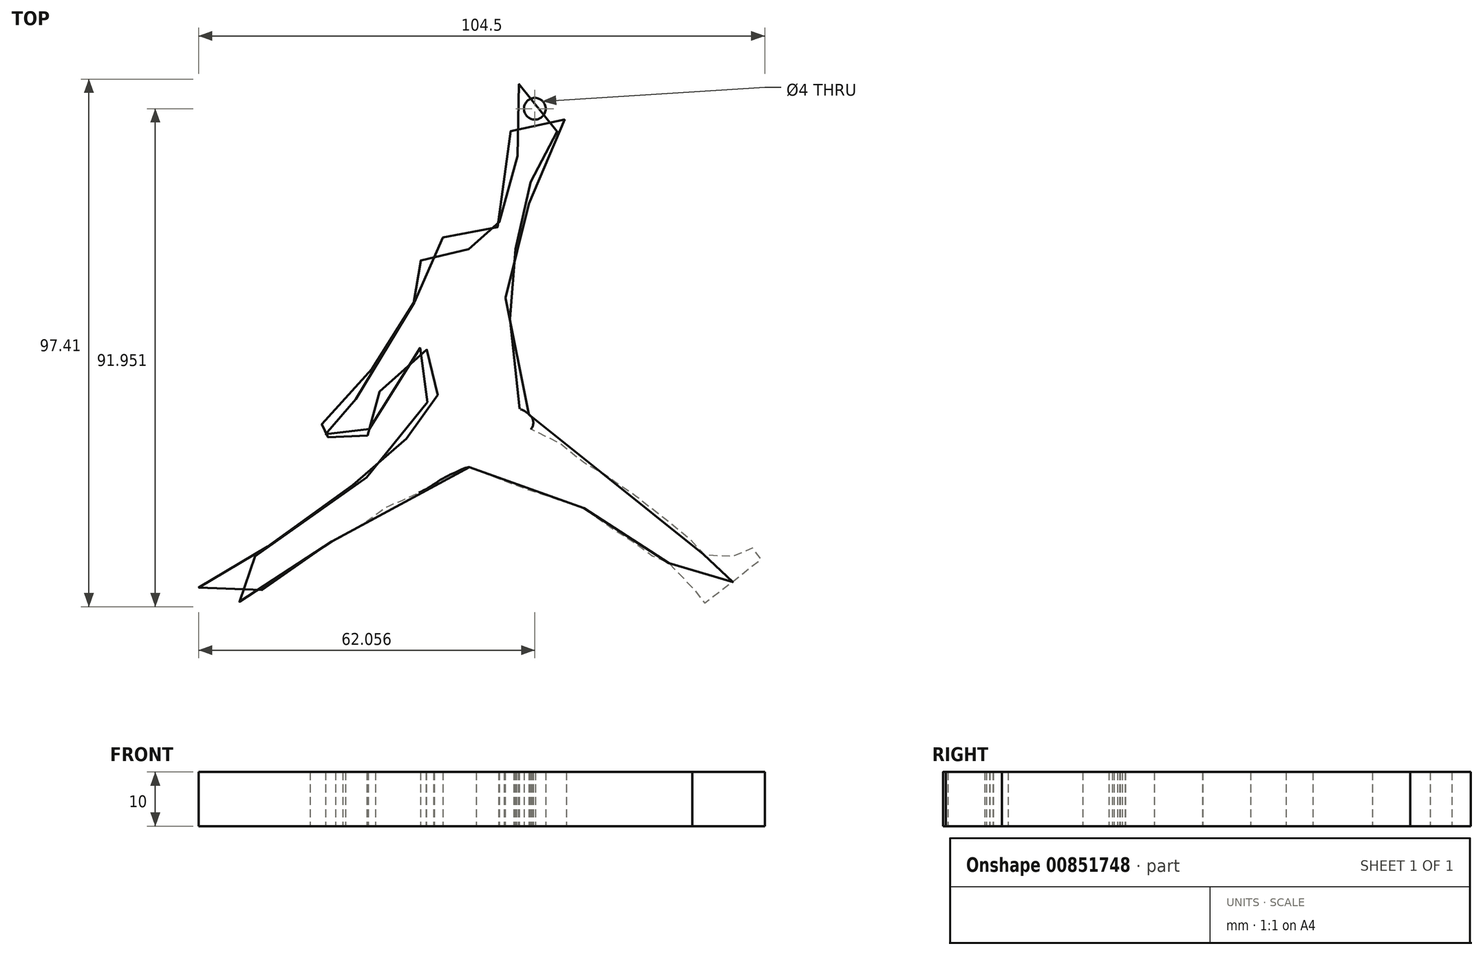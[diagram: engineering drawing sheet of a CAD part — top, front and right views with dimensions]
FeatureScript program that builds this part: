
annotation { "Feature Type Name" : "Feature", "Feature Type Description" : "" }
export const myFeature = defineFeature(function(context is Context, id is Id, definition is map)
    precondition{}
    {
        {
            var Q0;
            Q0=qCreatedBy(makeId("Top.planeOp"),FACE);
            var sketch = newSketch(context, id + "F0", { "sketchPlane" : qUnion([Q0])});
            skFitSpline(sketch, "E0", {"points": [v(0, -19.8) * mm, v(0.2, -19.83) * mm, v(0.48, -19.99) * mm, v(1.1, -20.32) * mm, v(2.32, -20.88) * mm, v(3.56, -21.27) * mm, v(5.27, -21.74) * mm, v(7.68, -22.78) * mm, v(9.68, -23.51) * mm, v(11.32, -24.32) * mm, v(13.95, -25.3) * mm, v(15.3, -25.56) * mm, v(18.19, -26.14) * mm, v(19.48, -26.44) * mm, v(19.57, -26.65) * mm, v(20.06, -26.91) * mm, v(21.05, -27.34) * mm, v(22.12, -27.94) * mm, v(23.74, -29.2) * mm, v(25.71, -30.67) * mm, v(27.3, -31.83) * mm, v(28.82, -33.03) * mm, v(29.33, -33.3) * mm, v(29.66, -33.44) * mm, v(30.19, -33.56) * mm, v(30.42, -33.56) * mm, v(31.1, -34.2) * mm, v(32.19, -34.96) * mm, v(33.13, -35.66) * mm, v(34.06, -36.37) * mm, v(34.75, -36.83) * mm, v(35.13, -36.98) * mm, v(35.58, -36.98) * mm, v(35.91, -36.98) * mm, v(36.16, -36.98) * mm, v(36.7, -37.44) * mm, v(37.25, -37.84) * mm, v(37.4, -38.04) * mm, v(37.53, -38.3) * mm, v(37.79, -38.55) * mm, v(38.11, -38.88) * mm, v(38.42, -39.16) * mm, v(38.8, -39.59) * mm, v(39.15, -39.72) * mm, v(39.3, -40) * mm, v(39.44, -40.32) * mm, v(40.42, -41.42) * mm, v(40.69, -41.76) * mm, v(41.12, -42) * mm, v(41.13, -42.31) * mm, v(41.37, -42.96) * mm, v(41.75, -43.62) * mm, v(42.58, -45) * mm, v(43.18, -45) * mm, v(44.19, -44.26) * mm, v(45.57, -43.07) * mm, v(47.18, -41.78) * mm, v(49.3, -40.67) * mm, v(51.32, -39.06) * mm, v(52.93, -37.54) * mm, v(54.5, -35.98) * mm, v(54.31, -35.5) * mm, v(53.92, -35.14) * mm, v(53.48, -34.9) * mm, v(52.87, -34.71) * mm, v(52.07, -34.83) * mm, v(51.46, -35.2) * mm, v(50.72, -35.63) * mm, v(50.03, -36.06) * mm, v(49.52, -36.26) * mm, v(48.35, -36.32) * mm, v(46.9, -36.34) * mm, v(45.76, -36.31) * mm, v(44.32, -36.3) * mm, v(43.12, -35.83) * mm, v(42.05, -34.72) * mm, v(41.47, -34.5) * mm, v(41.02, -34.03) * mm, v(40.88, -33.43) * mm, v(40.56, -33) * mm, v(39.17, -32.11) * mm, v(37.3, -30.2) * mm, v(36.82, -29.96) * mm, v(35.4, -28.76) * mm, v(33.62, -27.29) * mm, v(31.48, -25.76) * mm, v(29, -23.88) * mm, v(27.27, -22.71) * mm, v(25.08, -21.3) * mm, v(23.68, -20.35) * mm, v(23.38, -20.22) * mm, v(22.62, -20.12) * mm, v(21.98, -19.97) * mm, v(20.96, -18.83) * mm, v(19.69, -17.68) * mm, v(18.54, -16.8) * mm, v(17.36, -15.88) * mm, v(15.82, -14.96) * mm, v(14.2, -14.23) * mm, v(13, -13.6) * mm, v(11.37, -12.78) * mm, v(11.5, -12.6) * mm, v(11.63, -12.33) * mm, v(11.73, -12.03) * mm, v(11.78, -11.66) * mm, v(11.78, -11.43) * mm, v(11.72, -11.1) * mm, v(11.47, -10.57) * mm, v(11.04, -10.14) * mm, v(10.46, -9.65) * mm, v(9.6, -9.16) * mm, v(9.23, -9.02) * mm, v(8.92, -8.2) * mm, v(8.4, -7.03) * mm, v(8.55, -6.5) * mm, v(8.93, -4.45) * mm, v(9.15, -2.65) * mm, v(9.15, -0.27) * mm, v(9.04, 3.33) * mm, v(8.75, 5.3) * mm, v(7.8, 6.92) * mm, v(7.17, 8.5) * mm, v(6.73, 10.55) * mm, v(6.7, 11.32) * mm, v(6.63, 12.71) * mm, v(6.92, 13.58) * mm, v(7.53, 15) * mm, v(7.96, 16.47) * mm, v(8.12, 17.37) * mm, v(8.18, 18.32) * mm, v(8.17, 19) * mm, v(8.19, 19.73) * mm, v(8.4, 20.15) * mm, v(8.63, 20.9) * mm, v(8.65, 21.68) * mm, v(8.69, 22.57) * mm, v(9.04, 23.14) * mm, v(9.28, 23.9) * mm, v(9.63, 25.04) * mm, v(10.14, 27.67) * mm, v(10.56, 28.03) * mm, v(10.97, 28.41) * mm, v(10.97, 29.06) * mm, v(11.35, 30.86) * mm, v(11.47, 32.16) * mm, v(11.26, 32.93) * mm, v(11.38, 34.34) * mm, v(11.55, 35.53) * mm, v(11.75, 36.87) * mm, v(11.8, 37.9) * mm, v(12.08, 38.72) * mm, v(12.08, 39.7) * mm, v(11.8, 40.14) * mm, v(11.77, 40.47) * mm, v(11.97, 40.67) * mm, v(12.41, 40.67) * mm, v(13.83, 40.86) * mm, v(15.35, 41.58) * mm, v(16.46, 42.42) * mm, v(17.28, 43.69) * mm, v(17.85, 45.37) * mm, v(17.85, 46.66) * mm, v(17.7, 47.76) * mm, v(16.45, 50) * mm, v(14.85, 51.2) * mm, v(13.17, 51.76) * mm, v(11.4, 51.72) * mm, v(9.32, 51) * mm, v(7.84, 49.76) * mm, v(7.04, 48.07) * mm, v(6.52, 46.47) * mm, v(6.8, 44.8) * mm, v(7.12, 43.59) * mm, v(7.52, 42.5) * mm, v(7.92, 41.63) * mm, v(8.48, 40.63) * mm, v(8.8, 39.59) * mm, v(9, 38.7) * mm, v(8.8, 37.22) * mm, v(8.32, 35.02) * mm, v(8, 33.7) * mm, v(7.64, 33.68) * mm, v(7.49, 33.28) * mm, v(6.98, 31.54) * mm, v(6.42, 29.74) * mm, v(6.4, 29.36) * mm, v(6.52, 29.25) * mm, v(6.28, 28.69) * mm, v(5.8, 27.72) * mm, v(5.47, 26.9) * mm, v(5.43, 25.97) * mm, v(5.5, 25.32) * mm, v(4.93, 23.98) * mm, v(4.28, 21.56) * mm, v(3.93, 20.36) * mm, v(2.62, 19.25) * mm, v(1.97, 17.75) * mm, v(1.83, 18.14) * mm, v(1.6, 18.68) * mm, v(1.35, 18.93) * mm, v(1.25, 19.12) * mm, v(1.26, 19.84) * mm, v(1.16, 20) * mm, v(0.85, 20.1) * mm, v(0, 20.35) * mm, v(-0.12, 20.4) * mm, v(-0.3, 20.79) * mm, v(-0.65, 20.9) * mm, v(-0.93, 21) * mm, v(-1.4, 21.55) * mm, v(-2.02, 22.07) * mm, v(-2.8, 22.45) * mm, v(-3.7, 22.65) * mm, v(-4.58, 22.65) * mm, v(-5.6, 22.44) * mm, v(-5.99, 22.27) * mm, v(-6.86, 21.68) * mm, v(-7.56, 20.92) * mm, v(-8.27, 19.95) * mm, v(-9, 18.2) * mm, v(-8.94, 16.83) * mm, v(-8.44, 15.6) * mm, v(-7.7, 14.82) * mm, v(-7, 14.19) * mm, v(-6.7, 13.85) * mm, v(-6.6, 13.68) * mm, v(-6.76, 13.45) * mm, v(-6.84, 12.99) * mm, v(-6.96, 12.6) * mm, v(-7.42, 12.08) * mm, v(-8.13, 11.5) * mm, v(-8.53, 11.19) * mm, v(-8.97, 11.19) * mm, v(-9.5, 10.92) * mm, v(-10.2, 10.58) * mm, v(-10.93, 9.51) * mm, v(-11.95, 7.84) * mm, v(-12.98, 6.05) * mm, v(-13.52, 4.9) * mm, v(-13.7, 4.78) * mm, v(-14.25, 4.13) * mm, v(-14.77, 3.23) * mm, v(-15.14, 2.47) * mm, v(-15.35, 1.54) * mm, v(-15.93, 1.12) * mm, v(-17.56, -1.04) * mm, v(-18.35, -2.14) * mm, v(-19.01, -3.42) * mm, v(-20.12, -5.37) * mm, v(-20.55, -6.26) * mm, v(-20.93, -7.15) * mm, v(-21.08, -7.54) * mm, v(-21.83, -8.35) * mm, v(-22.7, -9.2) * mm, v(-23.65, -10.32) * mm, v(-25.58, -11.33) * mm, v(-26.46, -11.67) * mm, v(-28.16, -11.97) * mm, v(-29.17, -11.95) * mm, v(-29.43, -12.14) * mm, v(-29.32, -12.52) * mm, v(-29, -12.68) * mm, v(-27.78, -12.87) * mm, v(-26.67, -12.85) * mm, v(-25.56, -12.66) * mm, v(-24.78, -12.47) * mm, v(-24.7, -12.59) * mm, v(-24.87, -12.85) * mm, v(-25.4, -13.1) * mm, v(-25.98, -13.34) * mm, v(-26.48, -13.58) * mm, v(-26.53, -14) * mm, v(-26.24, -14.29) * mm, v(-25.72, -14.29) * mm, v(-24.7, -13.98) * mm, v(-23.6, -13.65) * mm, v(-22.87, -13.37) * mm, v(-22.96, -13.82) * mm, v(-23.2, -14.24) * mm, v(-23.36, -14.69) * mm, v(-23.05, -14.93) * mm, v(-22.32, -14.76) * mm, v(-21.54, -13.82) * mm, v(-20.95, -13.23) * mm, v(-20.53, -12.99) * mm, v(-20.12, -13.18) * mm, v(-19.86, -13.58) * mm, v(-19.18, -13.89) * mm, v(-18.45, -14) * mm, v(-17.79, -14) * mm, v(-17.43, -13.72) * mm, v(-17.38, -13.3) * mm, v(-17.64, -13.01) * mm, v(-18.33, -12.87) * mm, v(-18.7, -12.54) * mm, v(-18.92, -12) * mm, v(-18.68, -11.57) * mm, v(-18.87, -10.93) * mm, v(-18.85, -9.99) * mm, v(-18.42, -8.8) * mm, v(-17.71, -7.37) * mm, v(-17.02, -6.38) * mm, v(-16.6, -5.89) * mm, v(-15.45, -5.26) * mm, v(-13.94, -3.96) * mm, v(-12.68, -2.73) * mm, v(-11.66, -1.05) * mm, v(-10.86, 0.42) * mm, v(-10.74, 0.83) * mm, v(-10.32, 0.94) * mm, v(-9.56, 1.34) * mm, v(-9.27, 1.78) * mm, v(-8.99, 2.36) * mm, v(-8.7, 2.32) * mm, v(-8.16, 2.3) * mm, v(-7.93, 2.01) * mm, v(-7.62, 1.44) * mm, v(-7.2, 0.76) * mm, v(-6.8, 0.19) * mm, v(-6.56, -0.15) * mm, v(-6.51, -0.63) * mm, v(-6.5, -1.2) * mm, v(-6.23, -1.5) * mm, v(-5.87, -2) * mm, v(-5.69, -2.18) * mm, v(-5.6, -2.7) * mm, v(-5.39, -3.44) * mm, v(-5.2, -4.1) * mm, v(-4.96, -4.71) * mm, v(-4.88, -5.07) * mm, v(-5.35, -5.55) * mm, v(-5.75, -6.2) * mm, v(-5.9, -6.54) * mm, v(-6.45, -6.58) * mm, v(-6.95, -6.78) * mm, v(-7.52, -7.26) * mm, v(-7.82, -7.89) * mm, v(-8.02, -8.63) * mm, v(-8.02, -9.27) * mm, v(-8.07, -11.5) * mm, v(-8.53, -12.18) * mm, v(-9.13, -12.78) * mm, v(-9.73, -13.06) * mm, v(-10.45, -13.22) * mm, v(-10.95, -13.6) * mm, v(-11.33, -14.19) * mm, v(-11.53, -14.49) * mm, v(-12.87, -15.47) * mm, v(-14.13, -16.47) * mm, v(-15.42, -17.68) * mm, v(-16.6, -19.1) * mm, v(-17.56, -20.03) * mm, v(-18.21, -21.16) * mm, v(-18.58, -21.64) * mm, v(-18.96, -21.75) * mm, v(-19.47, -21.82) * mm, v(-20.07, -22.02) * mm, v(-20.92, -22.52) * mm, v(-21.49, -23.06) * mm, v(-21.94, -23.46) * mm, v(-24.7, -24.7) * mm, v(-28.08, -26.7) * mm, v(-30.64, -28.42) * mm, v(-32.43, -29.87) * mm, v(-33.58, -30.95) * mm, v(-35.47, -32.92) * mm, v(-36.76, -34.15) * mm, v(-38.14, -35.01) * mm, v(-39.62, -36.3) * mm, v(-40.97, -37.56) * mm, v(-42.2, -38.67) * mm, v(-43.45, -39.22) * mm, v(-44.68, -39.65) * mm, v(-45.7, -39.83) * mm, v(-46.8, -40.02) * mm, v(-48.3, -40.26) * mm, v(-49.8, -41.48) * mm, v(-49.93, -42.56) * mm, v(-49.26, -43.64) * mm, v(-47.97, -44.8) * mm, v(-46.76, -45.47) * mm, v(-44.93, -45.47) * mm, v(-43.58, -44.86) * mm, v(-42.36, -44.66) * mm, v(-41.07, -44.66) * mm, v(-39.86, -44.39) * mm, v(-38.98, -43.3) * mm, v(-38.37, -42.56) * mm, v(-37.76, -42.3) * mm, v(-37.02, -41.75) * mm, v(-36.27, -40.26) * mm, v(-35.33, -39.86) * mm, v(-34.51, -38.98) * mm, v(-33.77, -38.57) * mm, v(-32.55, -37.9) * mm, v(-32.14, -37.58) * mm, v(-31.84, -37.74) * mm, v(-31.3, -37.86) * mm, v(-30.89, -37.67) * mm, v(-30.39, -37.22) * mm, v(-25.67, -33.66) * mm, v(-25, -33.4) * mm, v(-22.17, -31.83) * mm, v(-19.98, -30.47) * mm, v(-17.05, -28.43) * mm, v(-15.38, -27.23) * mm, v(-13.6, -26.45) * mm, v(-9.74, -24.72) * mm, v(-7.28, -23.42) * mm, v(-4.62, -21.74) * mm, v(-2.1, -20.54) * mm, v(-0.7, -19.91) * mm, v(0, -19.8) * mm]});
            skSolve(sketch);
        }
        {
            var Q0;
            Q0=makeQuery(id+"F0.imprint","IMPRINT",FACE,{"disambiguationData":[TD([[makeQuery(id+"F0.imprint","IMPRINT",EDGE,{"derivedFrom":sQuery(id+"F0.wireOp",EDGE,"E0")}),1.0]])]});
            extrude(context, id + "F1", {"entities" : qUnion([Q0]), "depth" : 10 * mm});
        }
        {
            var Q0;
            Q0=qCreatedBy(makeId("Top.planeOp"),FACE);
            var sketch = newSketch(context, id + "F2", { "sketchPlane" : qUnion([Q0])});
            skCircle(sketch, "E1", {"center": v(12.07, 46.36) * mm, "radius": 3.34 * mm});
            skSolve(sketch);
        }
        {
            var Q0;
            Q0=sQuery(id+"F2.wireOp",VERTEX,"E1.center");
            var Q1;
            Q1=makeQuery(id+"F1.opExtrude","SWEPT_BODY",BODY,{"disambiguationData":[OSD([sQuery(id+"F0.wireOp",EDGE,"E0")])]});
            hole(context, id + "F3", {"style" : HoleStyle.SIMPLE, "endStyle" : HoleEndStyle.THROUGH, "oppositeDirection" : true, "holeDiameter" : 4 * mm, "majorDiameter" : 5 * mm, "isTappedThrough" : true, "tappedDepth" : 12 * mm, "tapClearance" : 3, "locations" : qUnion([Q0]), "scope" : qUnion([Q1])});
        }
    });
